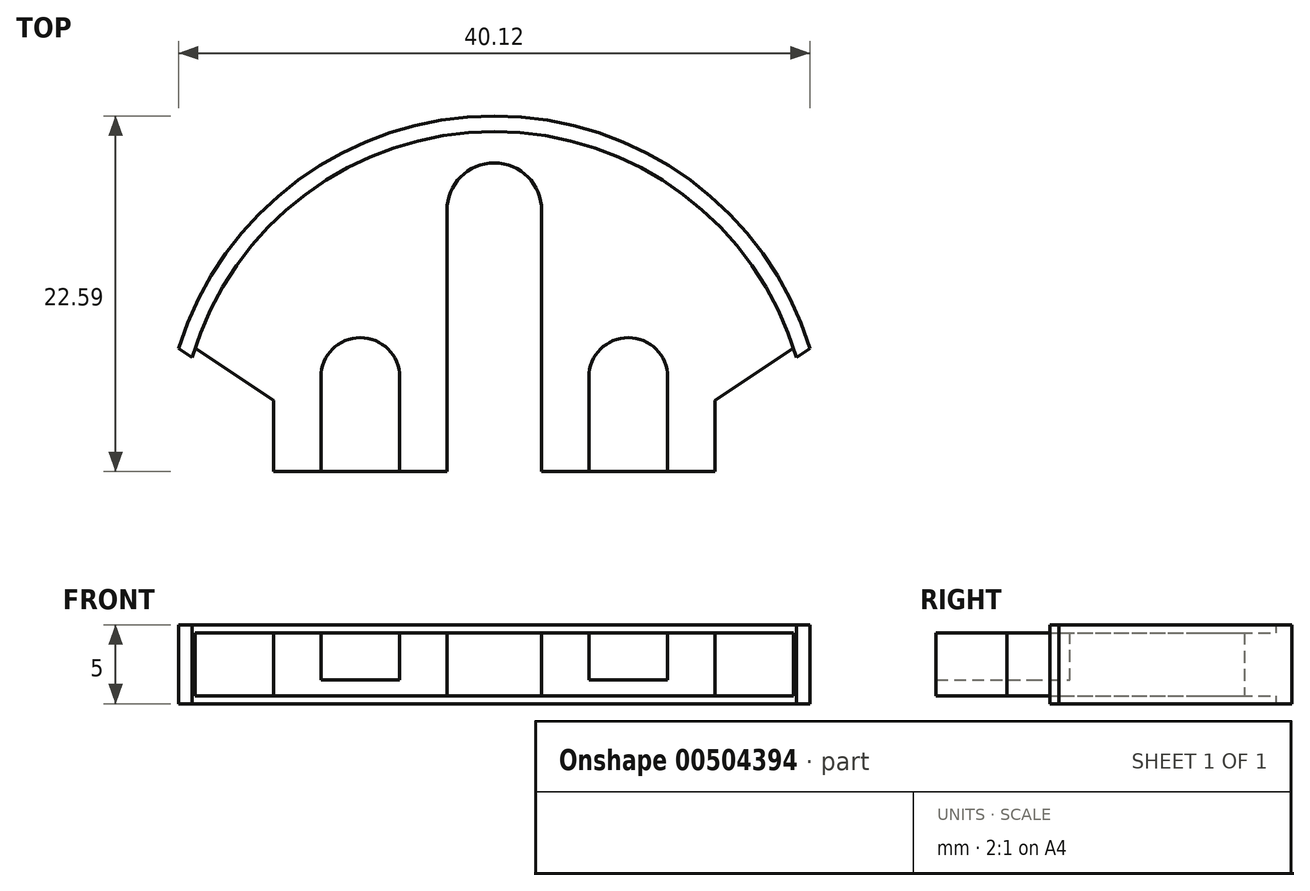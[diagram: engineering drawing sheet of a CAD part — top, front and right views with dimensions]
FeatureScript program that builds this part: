
annotation { "Feature Type Name" : "Feature", "Feature Type Description" : "" }
export const myFeature = defineFeature(function(context is Context, id is Id, definition is map)
    precondition{}
    {
        {
            var Q0;
            Q0=qCreatedBy(makeId("Top.planeOp"),FACE);
            var sketch = newSketch(context, id + "F0", { "sketchPlane" : qUnion([Q0])});
            skArc(sketch, "E0", {"start": v(19, 6.24) * mm, "mid": v(0, 20) * mm, "end": v(-19, 6.24) * mm});
            skLineSegment(sketch, "E1", {"start": v(-19, 6.24) * mm, "end": v(-14.01, 2.91) * mm});
            skLineSegment(sketch, "E2", {"start": v(-14.01, 2.91) * mm, "end": v(-14.01, -1.59) * mm});
            skLineSegment(sketch, "E3", {"start": v(-14.01, -1.59) * mm, "end": v(-3.01, -1.59) * mm});
            skLineSegment(sketch, "E4", {"start": v(-3.01, -1.59) * mm, "end": v(-3.01, 14.99) * mm});
            skArc(sketch, "E5", {"start": v(0, 18) * mm, "mid": v(-2.13, 17.12) * mm, "end": v(-3.01, 14.99) * mm});
            skLineSegment(sketch, "E6.MirrorCS", {"start": v(14.01, 2.91) * mm, "end": v(14.01, -1.59) * mm});
            skLineSegment(sketch, "E7.MirrorCS", {"start": v(3.01, -1.59) * mm, "end": v(3.01, 14.99) * mm});
            skLineSegment(sketch, "E8.MirrorCS", {"start": v(14.01, -1.59) * mm, "end": v(3.01, -1.59) * mm});
            skArc(sketch, "E9.MirrorCS", {"start": v(0, 18) * mm, "mid": v(2.13, 17.12) * mm, "end": v(3.01, 14.99) * mm});
            skLineSegment(sketch, "E10.trimOffspring", {"start": v(14.01, 2.91) * mm, "end": v(19, 6.24) * mm});
            skPoint(sketch, "E11.trimOffspring.end.orphan", {"position": v(0, -6.45) * mm});
            skSolve(sketch);
        }
        {
            var Q0;
            Q0 = qSketchRegion(id + "F0", true);
            extrude(context, id + "F1", {"entities" : qUnion([Q0]), "depth" : 2 * mm, "offsetDistance" : 25.4 * mm, "hasSecondDirection" : true, "secondDirectionOppositeDirection" : true, "secondDirectionDepth" : 2 * mm});
        }
        {
            var Q0;
            Q0=qCreatedBy(makeId("Top.planeOp"),FACE);
            var sketch = newSketch(context, id + "F2", { "sketchPlane" : qUnion([Q0])});
            skArc(sketch, "E12.0", {"start": v(20.06, 6.23) * mm, "mid": v(0, 21) * mm, "end": v(-20.06, 6.23) * mm});
            skArc(sketch, "E13.0", {"start": v(19.19, 5.64) * mm, "mid": v(0, 20) * mm, "end": v(-19.19, 5.64) * mm});
            skPoint(sketch, "E14.orphan", {"position": v(-19, 6.24) * mm});
            skPoint(sketch, "E15.orphan", {"position": v(19, 6.24) * mm});
            skLineSegment(sketch, "E16", {"start": v(-20.06, 6.23) * mm, "end": v(-19.19, 5.64) * mm});
            skLineSegment(sketch, "E17", {"start": v(19.19, 5.64) * mm, "end": v(20.06, 6.23) * mm});
            skSolve(sketch);
        }
        {
            var Q0;
            Q0 = qSketchRegion(id + "F2", true);
            extrude(context, id + "F3", {"entities" : qUnion([Q0]), "operationType" : NewBodyOperationType.ADD, "depth" : 2.5 * mm, "offsetDistance" : 25.4 * mm, "hasSecondDirection" : true, "secondDirectionOppositeDirection" : true, "secondDirectionDepth" : 2.5 * mm});
        }
        {
            var Q0;
            Q0=makeQuery(id+"F1.opExtrude","CAP_FACE",FACE,{"disambiguationData":[OSD([sQuery(id+"F0.wireOp",EDGE,"E0"),sQuery(id+"F0.wireOp",EDGE,"E1"),sQuery(id+"F0.wireOp",EDGE,"E2"),sQuery(id+"F0.wireOp",EDGE,"E3"),sQuery(id+"F0.wireOp",EDGE,"E4"),sQuery(id+"F0.wireOp",EDGE,"E5"),sQuery(id+"F0.wireOp",EDGE,"E6.MirrorCS"),sQuery(id+"F0.wireOp",EDGE,"E7.MirrorCS"),sQuery(id+"F0.wireOp",EDGE,"E8.MirrorCS"),sQuery(id+"F0.wireOp",EDGE,"E9.MirrorCS"),sQuery(id+"F0.wireOp",EDGE,"E10.trimOffspring")])],"isStart":false});
            var sketch = newSketch(context, id + "F4", { "sketchPlane" : qUnion([Q0])});
            skLineSegment(sketch, "E18", {"start": v(-11.01, -1.59) * mm, "end": v(-11.01, 4.41) * mm});
            skArc(sketch, "E19", {"start": v(-6.01, 4.41) * mm, "mid": v(-8.51, 6.91) * mm, "end": v(-11.01, 4.41) * mm});
            skLineSegment(sketch, "E20", {"start": v(-6.01, 4.41) * mm, "end": v(-6.01, -1.59) * mm});
            skLineSegment(sketch, "E21", {"start": v(-6.01, -1.59) * mm, "end": v(-11.01, -1.59) * mm});
            skLineSegment(sketch, "E22.MirrorCS", {"start": v(6.01, -1.59) * mm, "end": v(11.01, -1.59) * mm});
            skLineSegment(sketch, "E23.MirrorCS", {"start": v(11.01, -1.59) * mm, "end": v(11.01, 4.41) * mm});
            skLineSegment(sketch, "E24.MirrorCS", {"start": v(6.01, 4.41) * mm, "end": v(6.01, -1.59) * mm});
            skArc(sketch, "E25.MirrorCS", {"start": v(6.01, 4.41) * mm, "mid": v(8.51, 6.91) * mm, "end": v(11.01, 4.41) * mm});
            skSolve(sketch);
        }
        {
            var Q0;
            Q0 = qSketchRegion(id + "F4", true);
            extrude(context, id + "F5", {"entities" : qUnion([Q0]), "operationType" : NewBodyOperationType.REMOVE, "oppositeDirection" : true, "depth" : 3 * mm, "offsetDistance" : 25.4 * mm});
        }
    });
